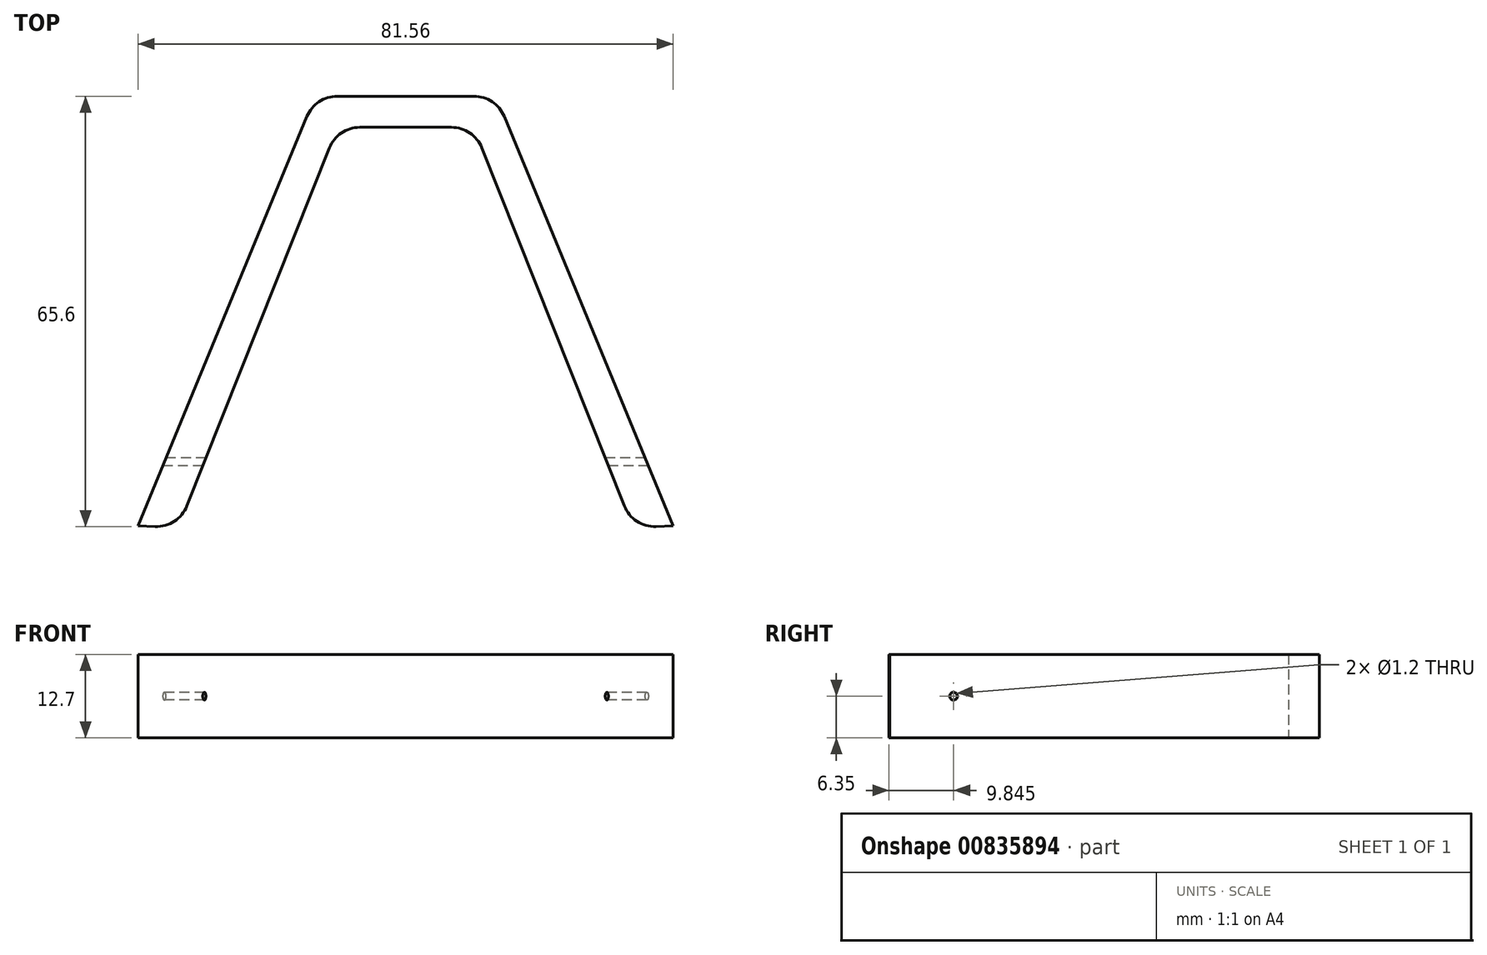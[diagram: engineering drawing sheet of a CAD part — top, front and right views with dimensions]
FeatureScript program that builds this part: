
annotation { "Feature Type Name" : "Feature", "Feature Type Description" : "" }
export const myFeature = defineFeature(function(context is Context, id is Id, definition is map)
    precondition{}
    {
        {
            var Q0;
            Q0=qCreatedBy(makeId("Top.planeOp"),FACE);
            var sketch = newSketch(context, id + "F0", { "sketchPlane" : qUnion([Q0])});
            skLineSegment(sketch, "E0", {"start": v(0, 34.22) * mm, "end": v(-10.36, 34.22) * mm});
            skLineSegment(sketch, "E1", {"start": v(-10.36, 34.22) * mm, "end": v(-34.64, -26.77) * mm});
            skLineSegment(sketch, "E2", {"start": v(0, 38.95) * mm, "end": v(-13.75, 38.95) * mm});
            skLineSegment(sketch, "E3", {"start": v(-13.75, 38.95) * mm, "end": v(-40.78, -26.55) * mm});
            skLineSegment(sketch, "E4", {"start": v(-40.78, -26.55) * mm, "end": v(-34.64, -26.77) * mm});
            skLineSegment(sketch, "E5", {"start": v(0, 38.95) * mm, "end": v(0, 34.22) * mm});
            skLineSegment(sketch, "E6.MirrorCS", {"start": v(0, 38.95) * mm, "end": v(13.75, 38.95) * mm});
            skLineSegment(sketch, "E7.MirrorCS", {"start": v(13.75, 38.95) * mm, "end": v(40.78, -26.55) * mm});
            skLineSegment(sketch, "E8.MirrorCS", {"start": v(0, 34.22) * mm, "end": v(10.36, 34.22) * mm});
            skLineSegment(sketch, "E9.MirrorCS", {"start": v(10.36, 34.22) * mm, "end": v(34.64, -26.77) * mm});
            skLineSegment(sketch, "E10.MirrorCS", {"start": v(40.78, -26.55) * mm, "end": v(34.64, -26.77) * mm});
            skSolve(sketch);
        }
        {
            var Q0;
            Q0=makeQuery(id+"F0.imprint","IMPRINT",FACE,{"disambiguationData":[TD([[makeQuery(id+"F0.imprint","IMPRINT",EDGE,{"derivedFrom":sQuery(id+"F0.wireOp",EDGE,"E0")}),-1.0]])]});
            var Q1;
            Q1=makeQuery(id+"F0.imprint","IMPRINT",FACE,{"disambiguationData":[TD([[makeQuery(id+"F0.imprint","IMPRINT",EDGE,{"derivedFrom":sQuery(id+"F0.wireOp",EDGE,"E5")}),1.0]])]});
            extrude(context, id + "F1", {"entities" : qUnion([Q0, Q1]), "depth" : 12.7 * mm, "offsetDistance" : 25.4 * mm});
        }
        {
            var Q0;
            Q0=qCreatedBy(makeId("Right.planeOp"),FACE);
            var sketch = newSketch(context, id + "F2", { "sketchPlane" : qUnion([Q0])});
            skCircle(sketch, "E11", {"center": v(-16.8, 6.35) * mm, "radius": 0.6 * mm});
            skPoint(sketch, "E11.centerSnap0", {"position": v(-26.55, 6.35) * mm});
            skSolve(sketch);
        }
        {
            var Q0;
            Q0=makeQuery(id+"F2.imprint","IMPRINT",FACE,{"disambiguationData":[TD([[makeQuery(id+"F2.imprint","IMPRINT",EDGE,{"derivedFrom":sQuery(id+"F2.wireOp",EDGE,"E11")}),1.0]])]});
            extrude(context, id + "F3", {"entities" : qUnion([Q0]), "operationType" : NewBodyOperationType.REMOVE, "depth" : 85.2 * mm, "offsetDistance" : 25 * mm, "hasSecondDirection" : true, "secondDirectionOppositeDirection" : true, "secondDirectionDepth" : 66 * mm});
        }
        {
            var Q0;
            Q0=makeQuery(id+"F1.opExtrude","SWEPT_EDGE",EDGE,{"disambiguationData":[OSD([sQuery(id+"F0.wireOp",EDGE,"E6.MirrorCS"),sQuery(id+"F0.wireOp",EDGE,"E7.MirrorCS")])]});
            var Q1;
            Q1=makeQuery(id+"F1.opExtrude","SWEPT_EDGE",EDGE,{"disambiguationData":[OSD([sQuery(id+"F0.wireOp",EDGE,"E2"),sQuery(id+"F0.wireOp",EDGE,"E3")])]});
            var Q2;
            Q2=makeQuery(id+"F1.opExtrude","SWEPT_EDGE",EDGE,{"disambiguationData":[OSD([sQuery(id+"F0.wireOp",EDGE,"E1"),sQuery(id+"F0.wireOp",EDGE,"E4")])]});
            var Q3;
            Q3=makeQuery(id+"F1.opExtrude","SWEPT_EDGE",EDGE,{"disambiguationData":[OSD([sQuery(id+"F0.wireOp",EDGE,"E9.MirrorCS"),sQuery(id+"F0.wireOp",EDGE,"E10.MirrorCS")])]});
            var Q4;
            Q4=makeQuery(id+"F1.opExtrude","SWEPT_EDGE",EDGE,{"disambiguationData":[OSD([sQuery(id+"F0.wireOp",EDGE,"E0"),sQuery(id+"F0.wireOp",EDGE,"E1")])]});
            var Q5;
            Q5=makeQuery(id+"F1.opExtrude","SWEPT_EDGE",EDGE,{"disambiguationData":[OSD([sQuery(id+"F0.wireOp",EDGE,"E8.MirrorCS"),sQuery(id+"F0.wireOp",EDGE,"E9.MirrorCS")])]});
            fillet(context, id + "F4", {"entities" : qUnion([Q0, Q1, Q2, Q3, Q4, Q5]), "radius" : 5 * mm, "tangentPropagation" : true, "allowEdgeOverflow" : false});
        }
    });
